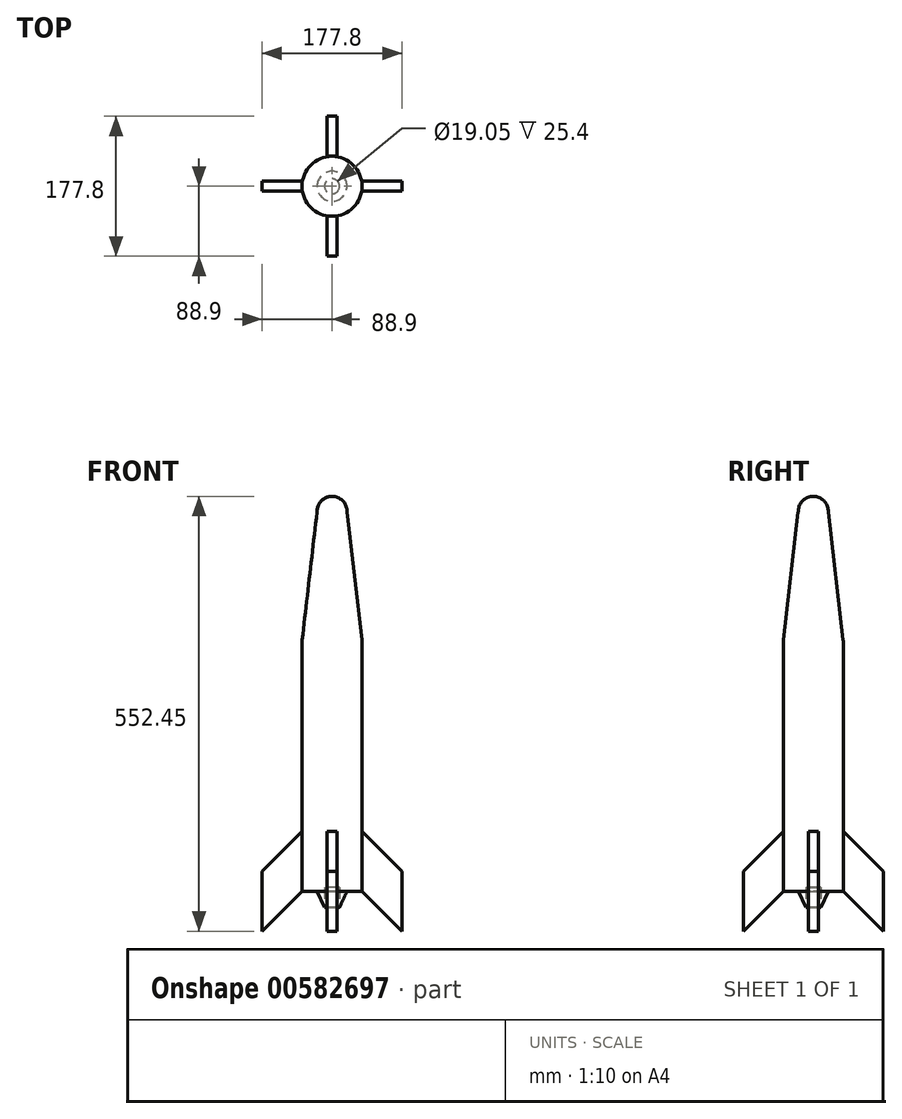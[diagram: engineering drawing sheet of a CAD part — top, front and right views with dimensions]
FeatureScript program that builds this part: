
annotation { "Feature Type Name" : "Feature", "Feature Type Description" : "" }
export const myFeature = defineFeature(function(context is Context, id is Id, definition is map)
    precondition{}
    {
        {
            var Q0;
            Q0=qCreatedBy(makeId("Front.planeOp"),FACE);
            var sketch = newSketch(context, id + "F0", { "sketchPlane" : qUnion([Q0])});
            skLineSegment(sketch, "E0", {"start": v(0, 0) * mm, "end": v(0, 330.2) * mm});
            skLineSegment(sketch, "E1", {"start": v(0, 330.2) * mm, "end": v(-38.1, 330.2) * mm});
            skLineSegment(sketch, "E2", {"start": v(-38.1, 330.2) * mm, "end": v(-38.1, 0) * mm});
            skLineSegment(sketch, "E3", {"start": v(-38.1, 0) * mm, "end": v(0, 0) * mm});
            skLineSegment(sketch, "E4.MirrorCS", {"start": v(0, 330.2) * mm, "end": v(38.1, 330.2) * mm});
            skLineSegment(sketch, "E5.MirrorCS", {"start": v(38.1, 330.2) * mm, "end": v(38.1, 0) * mm});
            skLineSegment(sketch, "E6.MirrorCS", {"start": v(38.1, 0) * mm, "end": v(0, 0) * mm});
            skArc(sketch, "E7", {"start": v(19.05, 330.2) * mm, "mid": v(0, 349.25) * mm, "end": v(-19.05, 330.2) * mm});
            skLineSegment(sketch, "E8", {"start": v(-38.1, 165.1) * mm, "end": v(-19.05, 330.2) * mm});
            skLineSegment(sketch, "E9", {"start": v(19.05, 330.2) * mm, "end": v(38.1, 165.1) * mm});
            skLineSegment(sketch, "E10", {"start": v(0, 330.2) * mm, "end": v(0, 349.25) * mm});
            skSolve(sketch);
        }
        {
            var Q0;
            {var subQ4=sQuery(id+"F0.wireOp",EDGE,"E0");Q0=makeQuery(id+"F0.imprint","IMPRINT",FACE,{"disambiguationData":[TD([[makeQuery(id+"F0.imprint","IMPRINT",EDGE,{"derivedFrom":subQ4}),1.0]])]});}
            var Q1;
            {var subQ0=sQuery(id+"F0.wireOp",EDGE,"E10");Q1=makeQuery(id+"F0.imprint","IMPRINT",FACE,{"disambiguationData":[TD([[makeQuery(id+"F0.imprint","IMPRINT",EDGE,{"derivedFrom":subQ0}),1.0]])]});}
            var Q2;
            Q2=sQuery(id+"F0.wireOp",EDGE,"E0");
            revolve(context, id + "F1", {"entities" : qUnion([Q0, Q1]), "axis" : qUnion([Q2]), "revolveType" : RevolveType.FULL});
        }
        {
            var Q0;
            Q0=makeQuery(id+"F1.opRevolve","SWEPT_EDGE",EDGE,{"disambiguationData":[OSD([sQuery(id+"F0.wireOp",EDGE,"E1"),sQuery(id+"F0.wireOp",EDGE,"E7"),sQuery(id+"F0.wireOp",EDGE,"E8")])]});
            var Q1;
            Q1=makeQuery(id+"F1.opRevolve","SWEPT_EDGE",EDGE,{"disambiguationData":[OSD([sQuery(id+"F0.wireOp",EDGE,"E2"),sQuery(id+"F0.wireOp",EDGE,"E8")])]});
            fillet(context, id + "F2", {"entities" : qUnion([Q0, Q1]), "radius" : 25.4 * mm, "tangentPropagation" : true, "allowEdgeOverflow" : false});
        }
        {
            var Q0;
            Q0=qCreatedBy(makeId("Front.planeOp"),FACE);
            var sketch = newSketch(context, id + "F3", { "sketchPlane" : qUnion([Q0])});
            skLineSegment(sketch, "E11.0", {"start": v(-38.1, 0) * mm, "end": v(0, 0) * mm});
            skLineSegment(sketch, "E11.1", {"start": v(38.1, 0) * mm, "end": v(0, 0) * mm});
            skLineSegment(sketch, "E12", {"start": v(-38.1, 0) * mm, "end": v(-38.1, -152.4) * mm});
            skLineSegment(sketch, "E13", {"start": v(-38.1, -152.4) * mm, "end": v(0, -152.4) * mm});
            skLineSegment(sketch, "E14", {"start": v(0, -152.4) * mm, "end": v(38.1, -152.4) * mm});
            skLineSegment(sketch, "E15", {"start": v(38.1, -152.4) * mm, "end": v(38.1, 0) * mm});
            skLineSegment(sketch, "E16", {"start": v(-19.05, -152.4) * mm, "end": v(-9.52, -172.83) * mm});
            skLineSegment(sketch, "E17", {"start": v(-9.52, -172.83) * mm, "end": v(9.53, -172.83) * mm});
            skLineSegment(sketch, "E18", {"start": v(9.53, -172.83) * mm, "end": v(19.05, -152.4) * mm});
            skLineSegment(sketch, "E19", {"start": v(0, 0) * mm, "end": v(0, -172.83) * mm});
            skLineSegment(sketch, "E20", {"start": v(-88.9, -127) * mm, "end": v(-88.9, -203.2) * mm});
            skLineSegment(sketch, "E21.MirrorCS", {"start": v(88.9, -203.2) * mm, "end": v(38.1, -152.4) * mm});
            skLineSegment(sketch, "E22.MirrorCS", {"start": v(88.9, -127) * mm, "end": v(88.9, -203.2) * mm});
            skLineSegment(sketch, "E23", {"start": v(38.1, -76.2) * mm, "end": v(88.9, -127) * mm});
            skLineSegment(sketch, "E24", {"start": v(-88.9, -127) * mm, "end": v(-38.1, -76.2) * mm});
            skLineSegment(sketch, "E25", {"start": v(-88.9, -203.2) * mm, "end": v(-38.1, -152.4) * mm});
            skSolve(sketch);
        }
        {
            var Q0;
            {var subQ5=sQuery(id+"F3.wireOp",EDGE,"E11.0");Q0=makeQuery(id+"F3.imprint","IMPRINT",FACE,{"disambiguationData":[TD([[makeQuery(id+"F3.imprint","IMPRINT",EDGE,{"derivedFrom":subQ5}),-1.0]])]});}
            var Q1;
            {var subQ3=sQuery(id+"F3.wireOp",EDGE,"E16");Q1=makeQuery(id+"F3.imprint","IMPRINT",FACE,{"disambiguationData":[TD([[makeQuery(id+"F3.imprint","IMPRINT",EDGE,{"derivedFrom":subQ3}),1.0]])]});}
            var Q2;
            Q2=sQuery(id+"F3.wireOp",EDGE,"E19");
            revolve(context, id + "F4", {"operationType" : NewBodyOperationType.ADD, "entities" : qUnion([Q0, Q1]), "axis" : qUnion([Q2]), "revolveType" : RevolveType.FULL});
        }
        {
            var Q0;
            {var subQ0=sQuery(id+"F3.wireOp",EDGE,"E21.MirrorCS");Q0=makeQuery(id+"F3.imprint","IMPRINT",FACE,{"disambiguationData":[TD([[makeQuery(id+"F3.imprint","IMPRINT",EDGE,{"derivedFrom":subQ0}),-1.0]])]});}
            var Q1;
            Q1=makeQuery(id+"F3.imprint","IMPRINT",FACE,{"disambiguationData":[TD([[makeQuery(id+"F3.imprint","IMPRINT",EDGE,{"derivedFrom":sQuery(id+"F3.wireOp",EDGE,"E20")}),1.0]])]});
            extrude(context, id + "F5", {"entities" : qUnion([Q0, Q1]), "operationType" : NewBodyOperationType.ADD, "endBound" : BoundingType.SYMMETRIC, "depth" : 12.7 * mm, "offsetDistance" : 25.4 * mm});
        }
        {
            var Q0;
            Q0=makeQuery(id+"F4.opRevolve","SWEPT_FACE",FACE,{"disambiguationData":[OSD([sQuery(id+"F3.wireOp",EDGE,"E17")])]});
            var sketch = newSketch(context, id + "F6", { "sketchPlane" : qUnion([Q0])});
            skCircle(sketch, "E26.0", {"center": v(0, 0) * mm, "radius": 9.53 * mm});
            skSolve(sketch);
        }
        {
            var Q0;
            Q0 = qSketchRegion(id + "F6", true);
            extrude(context, id + "F7", {"entities" : qUnion([Q0]), "operationType" : NewBodyOperationType.REMOVE, "oppositeDirection" : true, "depth" : 25.4 * mm, "offsetDistance" : 25.4 * mm});
        }
        {
            var Q0;
            Q0=qCreatedBy(makeId("Right.planeOp"),FACE);
            var sketch = newSketch(context, id + "F8", { "sketchPlane" : qUnion([Q0])});
            skLineSegment(sketch, "E27", {"start": v(-38.1, 0) * mm, "end": v(-38.1, -152.4) * mm});
            skLineSegment(sketch, "E28", {"start": v(-38.1, -152.4) * mm, "end": v(0, -152.4) * mm});
            skLineSegment(sketch, "E29", {"start": v(0, -152.4) * mm, "end": v(0, 0) * mm});
            skLineSegment(sketch, "E30", {"start": v(0, 0) * mm, "end": v(-38.1, 0) * mm});
            skLineSegment(sketch, "E31", {"start": v(-38.1, -76.2) * mm, "end": v(-88.9, -127) * mm});
            skLineSegment(sketch, "E32", {"start": v(-88.9, -127) * mm, "end": v(-88.9, -203.2) * mm});
            skLineSegment(sketch, "E33", {"start": v(-88.9, -203.2) * mm, "end": v(-38.1, -152.4) * mm});
            skLineSegment(sketch, "E34.MirrorCS", {"start": v(38.1, -76.2) * mm, "end": v(88.9, -127) * mm});
            skLineSegment(sketch, "E35.MirrorCS", {"start": v(88.9, -127) * mm, "end": v(88.9, -203.2) * mm});
            skLineSegment(sketch, "E36.MirrorCS", {"start": v(88.9, -203.2) * mm, "end": v(38.1, -152.4) * mm});
            skLineSegment(sketch, "E37", {"start": v(0, -152.4) * mm, "end": v(38.1, -152.4) * mm});
            skLineSegment(sketch, "E38", {"start": v(38.1, -152.4) * mm, "end": v(38.1, -76.2) * mm});
            skLineSegment(sketch, "E39", {"start": v(38.1, -76.2) * mm, "end": v(38.1, 0) * mm});
            skLineSegment(sketch, "E40", {"start": v(38.1, 0) * mm, "end": v(0, 0) * mm});
            skSolve(sketch);
        }
        {
            var Q0;
            {var subQ2=sQuery(id+"F8.wireOp",EDGE,"E31");Q0=makeQuery(id+"F8.imprint","IMPRINT",FACE,{"disambiguationData":[TD([[makeQuery(id+"F8.imprint","IMPRINT",EDGE,{"derivedFrom":subQ2}),1.0]])]});}
            var Q1;
            Q1=makeQuery(id+"F8.imprint","IMPRINT",FACE,{"disambiguationData":[TD([[makeQuery(id+"F8.imprint","IMPRINT",EDGE,{"derivedFrom":sQuery(id+"F8.wireOp",EDGE,"E34.MirrorCS")}),-1.0]])]});
            extrude(context, id + "F9", {"entities" : qUnion([Q0, Q1]), "endBound" : BoundingType.SYMMETRIC, "depth" : 12.7 * mm, "offsetDistance" : 25.4 * mm});
        }
    });
